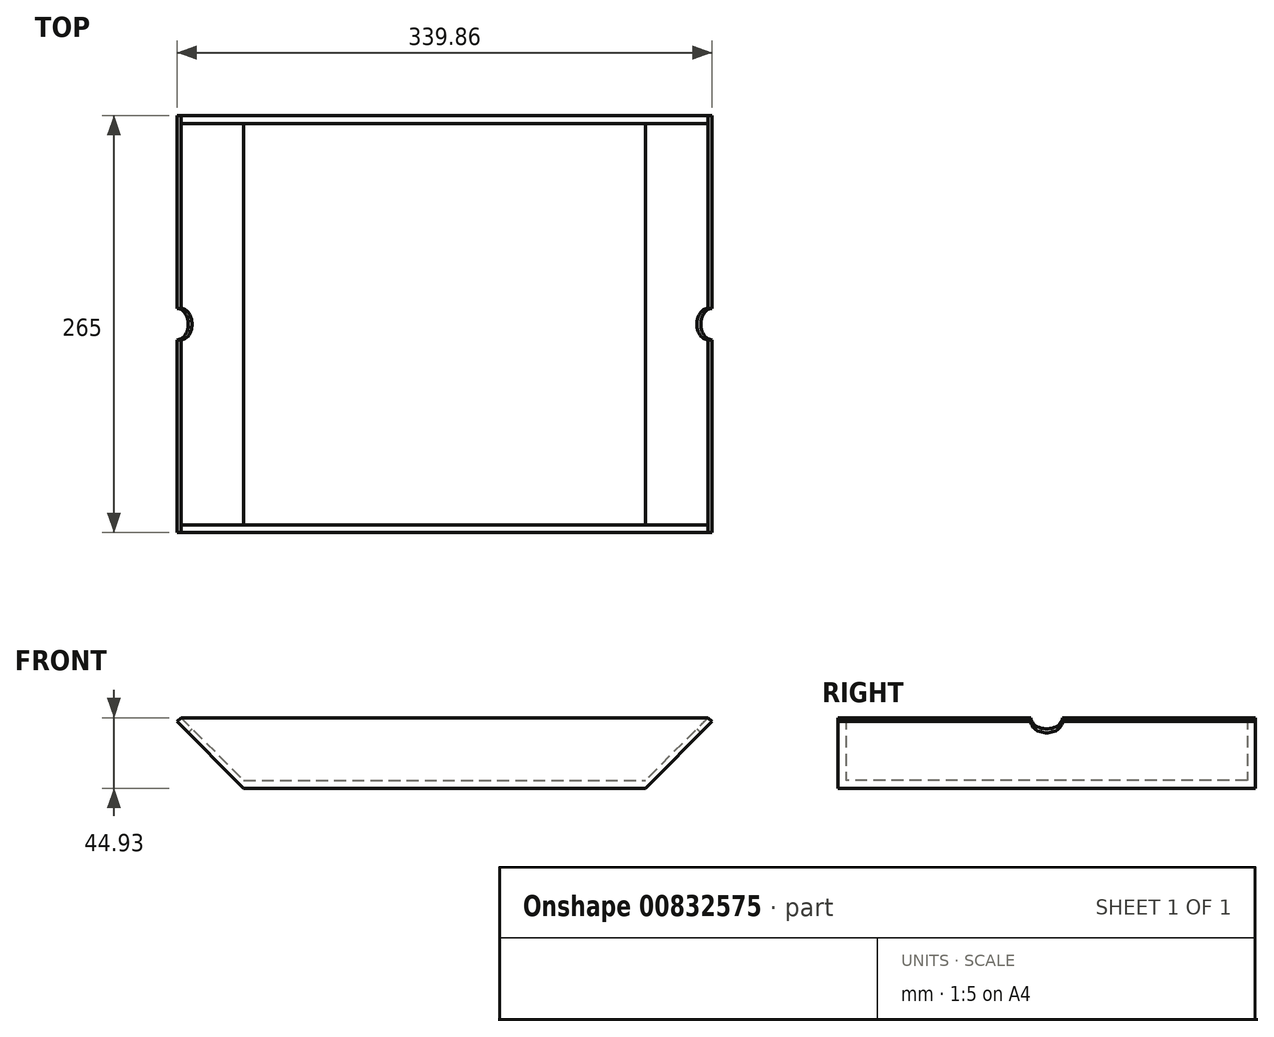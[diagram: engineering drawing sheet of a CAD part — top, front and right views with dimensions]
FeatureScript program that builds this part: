
annotation { "Feature Type Name" : "Feature", "Feature Type Description" : "" }
export const myFeature = defineFeature(function(context is Context, id is Id, definition is map)
    precondition{}
    {
        {
            var Q0;
            Q0=qCreatedBy(makeId("Top.planeOp"),FACE);
            var sketch = newSketch(context, id + "F0", { "sketchPlane" : qUnion([Q0])});
            skLineSegment(sketch, "E0.bottom", {"start": v(-127.5, 132.5) * mm, "end": v(127.5, 132.5) * mm});
            skLineSegment(sketch, "E0.top", {"start": v(-127.5, -132.5) * mm, "end": v(127.5, -132.5) * mm});
            skLineSegment(sketch, "E0.left", {"start": v(-127.5, 132.5) * mm, "end": v(-127.5, -132.5) * mm});
            skLineSegment(sketch, "E0.right", {"start": v(127.5, 132.5) * mm, "end": v(127.5, -132.5) * mm});
            skPoint(sketch, "E0.middle", {"position": v(0, 0) * mm});
            skSolve(sketch);
        }
        {
            var Q0;
            Q0=makeQuery(id+"F0.imprint","IMPRINT",FACE,{"disambiguationData":[TD([[makeQuery(id+"F0.imprint","IMPRINT",EDGE,{"derivedFrom":sQuery(id+"F0.wireOp",EDGE,"E0.bottom")}),-1.0]])]});
            extrude(context, id + "F1", {"entities" : qUnion([Q0]), "depth" : 5 * mm, "offsetDistance" : 25 * mm});
        }
        {
            var Q0;
            Q0=makeQuery(id+"F1.opExtrude","SWEPT_FACE",FACE,{"disambiguationData":[OSD([sQuery(id+"F0.wireOp",EDGE,"E0.top")])]});
            var sketch = newSketch(context, id + "F2", { "sketchPlane" : qUnion([Q0])});
            skLineSegment(sketch, "E1", {"start": v(127.5, 0) * mm, "end": v(169.93, 42.43) * mm});
            skLineSegment(sketch, "E2", {"start": v(169.93, 42.43) * mm, "end": v(167.43, 44.93) * mm});
            skLineSegment(sketch, "E3", {"start": v(167.43, 44.93) * mm, "end": v(127.5, 5) * mm});
            skLineSegment(sketch, "E4.MirrorCS", {"start": v(-169.93, 42.43) * mm, "end": v(-167.43, 44.93) * mm});
            skLineSegment(sketch, "E5.MirrorCS", {"start": v(-167.43, 44.93) * mm, "end": v(-127.5, 5) * mm});
            skLineSegment(sketch, "E6.MirrorCS", {"start": v(-127.5, 0) * mm, "end": v(-169.93, 42.43) * mm});
            skSolve(sketch);
        }
        {
            var Q0;
            Q0=makeQuery(id+"F2.imprint","IMPRINT",FACE,{"disambiguationData":[TD([[makeQuery(id+"F2.imprint","IMPRINT",EDGE,{"derivedFrom":sQuery(id+"F2.wireOp",EDGE,"E4.MirrorCS")}),-1.0]])]});
            var Q1;
            Q1=makeQuery(id+"F2.imprint","IMPRINT",FACE,{"disambiguationData":[TD([[makeQuery(id+"F2.imprint","IMPRINT",EDGE,{"derivedFrom":sQuery(id+"F2.wireOp",EDGE,"E1")}),1.0]])]});
            extrude(context, id + "F3", {"entities" : qUnion([Q0, Q1]), "operationType" : NewBodyOperationType.ADD, "oppositeDirection" : true, "depth" : 265 * mm, "offsetDistance" : 25 * mm});
        }
        {
            var Q0;
            Q0=makeQuery(id+"F3.opExtrude","SWEPT_FACE",FACE,{"disambiguationData":[OSD([sQuery(id+"F2.wireOp",EDGE,"E5.MirrorCS")])]});
            var sketch = newSketch(context, id + "F4", { "sketchPlane" : qUnion([Q0])});
            skCircle(sketch, "E7", {"center": v(0, 150.16) * mm, "radius": 10 * mm});
            skSolve(sketch);
        }
        {
            var Q0;
            Q0 = qSketchRegion(id + "F4", true);
            extrude(context, id + "F5", {"entities" : qUnion([Q0]), "operationType" : NewBodyOperationType.REMOVE, "oppositeDirection" : true, "depth" : 25 * mm, "offsetDistance" : 25 * mm});
        }
        {
            var Q0;
            Q0=makeQuery(id+"F3.opExtrude","SWEPT_FACE",FACE,{"disambiguationData":[OSD([sQuery(id+"F2.wireOp",EDGE,"E3")])]});
            var sketch = newSketch(context, id + "F6", { "sketchPlane" : qUnion([Q0])});
            skCircle(sketch, "E8", {"center": v(0, 150.16) * mm, "radius": 10 * mm});
            skSolve(sketch);
        }
        {
            var Q0;
            {var subQ0=sQuery(id+"F6.wireOp",EDGE,"E8");var subQ1=makeQuery(id+"F3.opExtrude","SWEPT_EDGE",EDGE,{"disambiguationData":[OSD([sQuery(id+"F2.wireOp",EDGE,"E2"),sQuery(id+"F2.wireOp",EDGE,"E3")])]});var subQ2=makeQuery(id+"F6.imprint","INTERSECT",VERTEX,{"disambiguationData":[OD(0.0)],"derivedFrom":[subQ1,subQ0]});Q0=makeQuery(id+"F6.imprint","IMPRINT",FACE,{"disambiguationData":[TD([[makeQuery(id+"F6.imprint","IMPRINT",EDGE,{"disambiguationData":[TD([[subQ2,1.0]])],"derivedFrom":subQ0}),1.0]])]});}
            extrude(context, id + "F7", {"entities" : qUnion([Q0]), "operationType" : NewBodyOperationType.REMOVE, "oppositeDirection" : true, "depth" : 25 * mm, "offsetDistance" : 25 * mm});
        }
        {
            var Q0;
            {var subQ0=sQuery(id+"F0.wireOp",EDGE,"E0.top");Q0=makeQuery(id+"F3.boolean.opBoolean","MERGE",FACE,{"derivedFrom":[makeQuery(id+"F1.opExtrude","SWEPT_FACE",FACE,{"disambiguationData":[OSD([subQ0])]}),makeQuery(id+"F3.opExtrude","CAP_FACE",FACE,{"disambiguationData":[OSD([subQ0,sQuery(id+"F0.wireOp",EDGE,"E0.right"),sQuery(id+"F2.wireOp",EDGE,"E1"),sQuery(id+"F2.wireOp",EDGE,"E2"),sQuery(id+"F2.wireOp",EDGE,"E3")])],"isStart":true}),makeQuery(id+"F3.opExtrude","CAP_FACE",FACE,{"disambiguationData":[OSD([subQ0,sQuery(id+"F0.wireOp",EDGE,"E0.left"),sQuery(id+"F2.wireOp",EDGE,"E4.MirrorCS"),sQuery(id+"F2.wireOp",EDGE,"E5.MirrorCS"),sQuery(id+"F2.wireOp",EDGE,"E6.MirrorCS")])],"isStart":true})]});}
            var sketch = newSketch(context, id + "F8", { "sketchPlane" : qUnion([Q0])});
            skLineSegment(sketch, "E9", {"start": v(-167.43, 44.93) * mm, "end": v(-169.93, 42.43) * mm});
            skLineSegment(sketch, "E10", {"start": v(-169.93, 42.43) * mm, "end": v(-127.5, 0) * mm});
            skLineSegment(sketch, "E11", {"start": v(-127.5, 0) * mm, "end": v(127.5, 0) * mm});
            skLineSegment(sketch, "E12", {"start": v(127.5, 0) * mm, "end": v(169.93, 42.43) * mm});
            skLineSegment(sketch, "E13", {"start": v(169.93, 42.43) * mm, "end": v(167.43, 44.93) * mm});
            skLineSegment(sketch, "E14", {"start": v(167.43, 44.93) * mm, "end": v(-167.43, 44.93) * mm});
            skSolve(sketch);
        }
        {
            var Q0;
            Q0=makeQuery(id+"F8.imprint","IMPRINT",FACE,{"disambiguationData":[TD([[makeQuery(id+"F8.imprint","IMPRINT",EDGE,{"derivedFrom":sQuery(id+"F8.wireOp",EDGE,"E14")}),1.0]])]});
            extrude(context, id + "F9", {"entities" : qUnion([Q0]), "operationType" : NewBodyOperationType.ADD, "oppositeDirection" : true, "depth" : 5 * mm, "offsetDistance" : 25 * mm});
        }
        {
            var Q0;
            {var subQ0=sQuery(id+"F0.wireOp",EDGE,"E0.top");Q0=makeQuery(id+"F3.boolean.opBoolean","MERGE",FACE,{"derivedFrom":[makeQuery(id+"F1.opExtrude","SWEPT_FACE",FACE,{"disambiguationData":[OSD([sQuery(id+"F0.wireOp",EDGE,"E0.bottom")])]}),makeQuery(id+"F3.opExtrude","CAP_FACE",FACE,{"disambiguationData":[OSD([subQ0,sQuery(id+"F0.wireOp",EDGE,"E0.right"),sQuery(id+"F2.wireOp",EDGE,"E1"),sQuery(id+"F2.wireOp",EDGE,"E2"),sQuery(id+"F2.wireOp",EDGE,"E3")])],"isStart":false}),makeQuery(id+"F3.opExtrude","CAP_FACE",FACE,{"disambiguationData":[OSD([subQ0,sQuery(id+"F0.wireOp",EDGE,"E0.left"),sQuery(id+"F2.wireOp",EDGE,"E4.MirrorCS"),sQuery(id+"F2.wireOp",EDGE,"E5.MirrorCS"),sQuery(id+"F2.wireOp",EDGE,"E6.MirrorCS")])],"isStart":false})]});}
            var sketch = newSketch(context, id + "F10", { "sketchPlane" : qUnion([Q0])});
            skLineSegment(sketch, "E15", {"start": v(-167.43, 44.93) * mm, "end": v(-169.93, 42.43) * mm});
            skLineSegment(sketch, "E16", {"start": v(-169.93, 42.43) * mm, "end": v(-127.5, 0) * mm});
            skLineSegment(sketch, "E17", {"start": v(-127.5, 0) * mm, "end": v(127.5, 0) * mm});
            skLineSegment(sketch, "E18", {"start": v(127.5, 0) * mm, "end": v(169.93, 42.43) * mm});
            skLineSegment(sketch, "E19", {"start": v(169.93, 42.43) * mm, "end": v(167.43, 44.93) * mm});
            skLineSegment(sketch, "E20", {"start": v(167.43, 44.93) * mm, "end": v(-167.43, 44.93) * mm});
            skSolve(sketch);
        }
        {
            var Q0;
            Q0=makeQuery(id+"F10.imprint","IMPRINT",FACE,{"disambiguationData":[TD([[makeQuery(id+"F10.imprint","IMPRINT",EDGE,{"derivedFrom":sQuery(id+"F10.wireOp",EDGE,"E20")}),1.0]])]});
            extrude(context, id + "F11", {"entities" : qUnion([Q0]), "operationType" : NewBodyOperationType.ADD, "oppositeDirection" : true, "depth" : 5 * mm, "offsetDistance" : 25 * mm});
        }
    });
